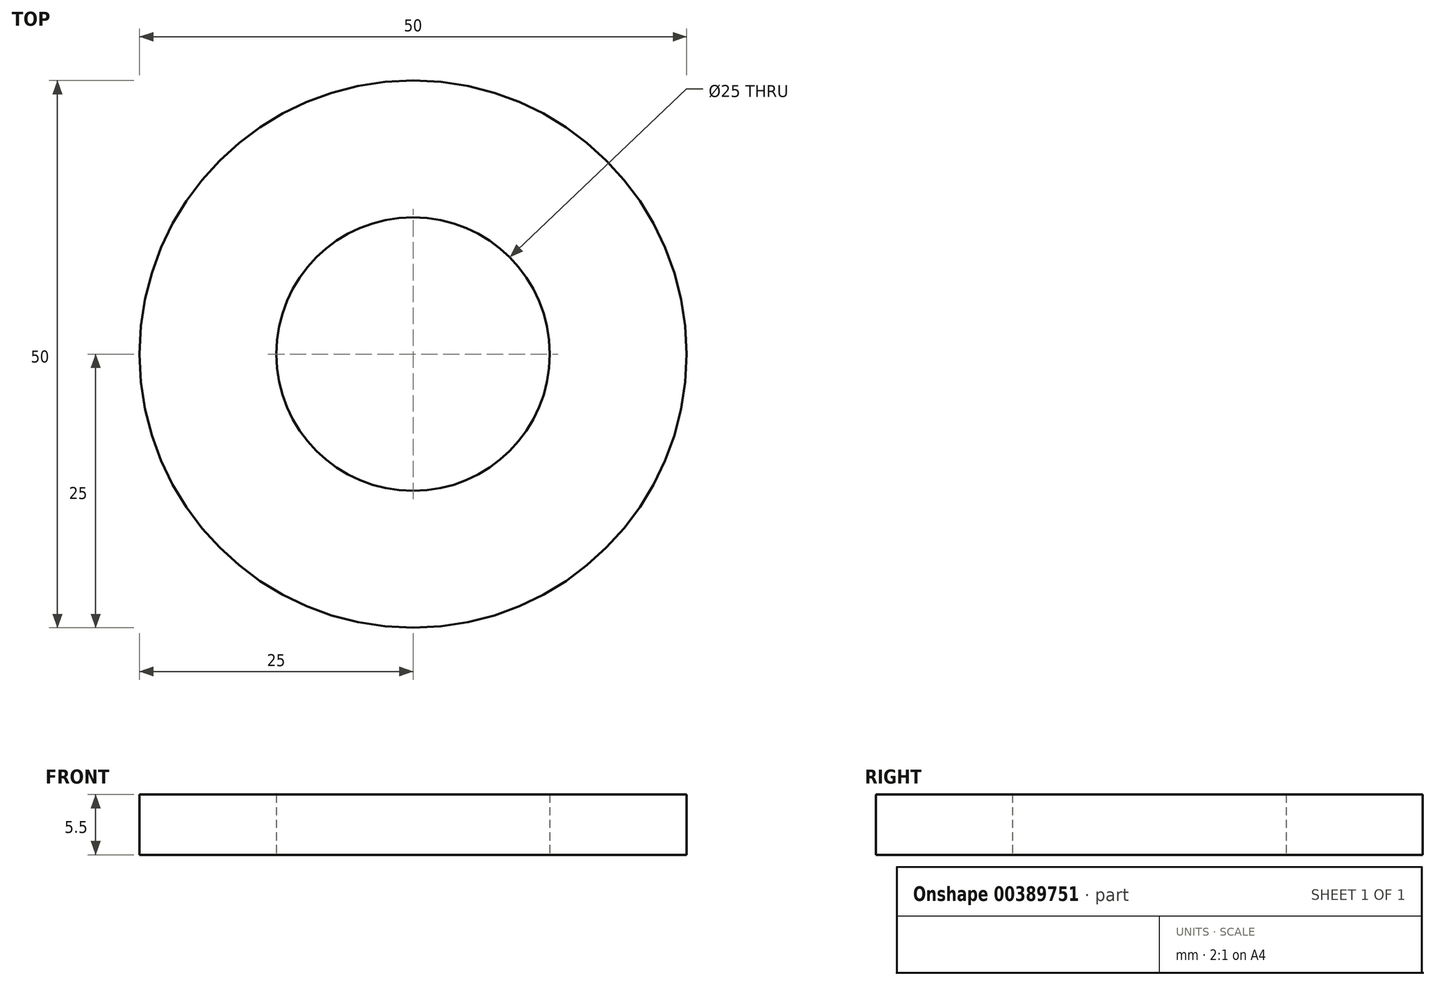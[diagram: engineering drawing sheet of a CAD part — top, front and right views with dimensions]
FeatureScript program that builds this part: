
annotation { "Feature Type Name" : "Feature", "Feature Type Description" : "" }
export const myFeature = defineFeature(function(context is Context, id is Id, definition is map)
    precondition{}
    {
        {
            var Q0;
            Q0=qCreatedBy(makeId("Top.planeOp"),FACE);
            var sketch = newSketch(context, id + "F0", { "sketchPlane" : qUnion([Q0])});
            skLineSegment(sketch, "E0.bottom", {"start": v(50, -17.5) * mm, "end": v(-50, -17.5) * mm});
            skLineSegment(sketch, "E0.top", {"start": v(50, 17.5) * mm, "end": v(-50, 17.5) * mm});
            skLineSegment(sketch, "E0.left", {"start": v(50, -17.5) * mm, "end": v(50, 17.5) * mm});
            skLineSegment(sketch, "E0.right", {"start": v(-50, -17.5) * mm, "end": v(-50, 17.5) * mm});
            skPoint(sketch, "E0.middle", {"position": v(0, 0) * mm});
            skSolve(sketch);
        }
        {
            var Q0;
            Q0=makeQuery(id+"F0.imprint","IMPRINT",FACE,{"disambiguationData":[TD([[makeQuery(id+"F0.imprint","IMPRINT",EDGE,{"derivedFrom":sQuery(id+"F0.wireOp",EDGE,"E0.bottom")}),-1.0]])]});
            extrude(context, id + "F1", {"entities" : qUnion([Q0]), "depth" : -18 * mm});
        }
        {
            var Q0;
            Q0=makeQuery(id+"F1.opExtrude","CAP_FACE",FACE,{"disambiguationData":[OSD([sQuery(id+"F0.wireOp",EDGE,"E0.bottom"),sQuery(id+"F0.wireOp",EDGE,"E0.top"),sQuery(id+"F0.wireOp",EDGE,"E0.left"),sQuery(id+"F0.wireOp",EDGE,"E0.right")])],"isStart":true});
            var sketch = newSketch(context, id + "F2", { "sketchPlane" : qUnion([Q0])});
            skCircle(sketch, "E1", {"center": v(0, 0) * mm, "radius": 12.7 * mm});
            skSolve(sketch);
        }
        {
            var Q0;
            Q0=makeQuery(id+"F2.imprint","IMPRINT",FACE,{"disambiguationData":[TD([[makeQuery(id+"F2.imprint","IMPRINT",EDGE,{"derivedFrom":sQuery(id+"F2.wireOp",EDGE,"E1")}),1.0]])]});
            extrude(context, id + "F3", {"entities" : qUnion([Q0]), "operationType" : NewBodyOperationType.ADD, "depth" : 19 * mm});
        }
        {
            var Q0;
            Q0=makeQuery(id+"F3.opExtrude","CAP_FACE",FACE,{"disambiguationData":[OSD([sQuery(id+"F2.wireOp",EDGE,"E1")])],"isStart":false});
            var sketch = newSketch(context, id + "F4", { "sketchPlane" : qUnion([Q0])});
            skCircle(sketch, "E2", {"center": v(0, 0) * mm, "radius": 25 * mm});
            skSolve(sketch);
        }
        {
            var Q0;
            Q0=makeQuery(id+"F4.imprint","IMPRINT",FACE,{"disambiguationData":[TD([[makeQuery(id+"F4.imprint","IMPRINT",EDGE,{"derivedFrom":sQuery(id+"F4.wireOp",EDGE,"E2")}),1.0]])]});
            var Q1;
            Q1=makeQuery(id+"F4.imprint","IMPRINT",FACE,{"disambiguationData":[TD([[makeQuery(id+"F4.imprint","IMPRINT",EDGE,{"derivedFrom":makeQuery(id+"F3.opExtrude","CAP_EDGE",EDGE,{"disambiguationData":[OSD([sQuery(id+"F2.wireOp",EDGE,"E1")])],"isStart":false})}),1.0]])]});
            extrude(context, id + "F5", {"entities" : qUnion([Q0, Q1]), "operationType" : NewBodyOperationType.ADD, "depth" : 5.5 * mm});
        }
        {
            var Q0;
            Q0=makeQuery(id+"F5.opExtrude","CAP_FACE",FACE,{"disambiguationData":[OSD([sQuery(id+"F4.wireOp",EDGE,"E2")])],"isStart":false});
            var sketch = newSketch(context, id + "F6", { "sketchPlane" : qUnion([Q0])});
            skCircle(sketch, "E3", {"center": v(0, 0) * mm, "radius": 2.5 * mm});
            skSolve(sketch);
        }
        {
            var Q0;
            Q0=qSketchRegion(id+"F6",true);
            extrude(context, id + "F7", {"entities" : qUnion([Q0]), "operationType" : NewBodyOperationType.ADD, "depth" : 3 * mm});
        }
        {
            var Q0;
            Q0=makeQuery(id+"F1.opExtrude","SWEPT_FACE",FACE,{"disambiguationData":[OSD([sQuery(id+"F0.wireOp",EDGE,"E0.bottom")])]});
            var sketch = newSketch(context, id + "F8", { "sketchPlane" : qUnion([Q0])});
            skLineSegment(sketch, "E4.bottom", {"start": v(-50, 0) * mm, "end": v(50, 0) * mm});
            skLineSegment(sketch, "E4.top", {"start": v(-50, -75) * mm, "end": v(50, -75) * mm});
            skLineSegment(sketch, "E4.left", {"start": v(-50, 0) * mm, "end": v(-50, -75) * mm});
            skLineSegment(sketch, "E4.right", {"start": v(50, 0) * mm, "end": v(50, -75) * mm});
            skSolve(sketch);
        }
        {
            var Q0;
            {var subQ0=sQuery(id+"F8.wireOp",EDGE,"E4.top");Q0=makeQuery(id+"F8.imprint","IMPRINT",FACE,{"disambiguationData":[TD([[makeQuery(id+"F8.imprint","IMPRINT",EDGE,{"derivedFrom":subQ0}),1.0]])]});}
            var Q1;
            {var subQ0=sQuery(id+"F8.wireOp",EDGE,"E4.bottom");Q1=makeQuery(id+"F8.imprint","IMPRINT",FACE,{"disambiguationData":[TD([[makeQuery(id+"F8.imprint","IMPRINT",EDGE,{"derivedFrom":subQ0}),1.0]])]});}
            extrude(context, id + "F9", {"entities" : qUnion([Q0, Q1]), "operationType" : NewBodyOperationType.ADD, "depth" : 12 * mm});
        }
        {
            var Q0;
            Q0=makeQuery(id+"F9.opExtrude","CAP_FACE",FACE,{"disambiguationData":[OSD([sQuery(id+"F8.wireOp",EDGE,"E4.bottom"),sQuery(id+"F8.wireOp",EDGE,"E4.top"),sQuery(id+"F8.wireOp",EDGE,"E4.left"),sQuery(id+"F8.wireOp",EDGE,"E4.right")])],"isStart":false});
            var sketch = newSketch(context, id + "F10", { "sketchPlane" : qUnion([Q0])});
            skLineSegment(sketch, "E5", {"start": v(0, 0) * mm, "end": v(-37.5, 0) * mm});
            skLineSegment(sketch, "E6", {"start": v(-37.5, 0) * mm, "end": v(-37.5, -50) * mm});
            skLineSegment(sketch, "E7", {"start": v(-37.5, -50) * mm, "end": v(37.5, -50) * mm});
            skLineSegment(sketch, "E8", {"start": v(37.5, -50) * mm, "end": v(37.5, 0) * mm});
            skLineSegment(sketch, "E9", {"start": v(37.5, 0) * mm, "end": v(0, 0) * mm});
            skLineSegment(sketch, "E10", {"start": v(50, 0) * mm, "end": v(50, -75) * mm});
            skLineSegment(sketch, "E11", {"start": v(50, -75) * mm, "end": v(-50, -75) * mm});
            skLineSegment(sketch, "E12", {"start": v(-50, -75) * mm, "end": v(-50, 0) * mm});
            skLineSegment(sketch, "E13", {"start": v(-50, 0) * mm, "end": v(50, 0) * mm});
            skSolve(sketch);
        }
        {
            var Q0;
            {var subQ2=sQuery(id+"F10.wireOp",EDGE,"E6");Q0=makeQuery(id+"F10.imprint","IMPRINT",FACE,{"disambiguationData":[TD([[makeQuery(id+"F10.imprint","IMPRINT",EDGE,{"derivedFrom":subQ2}),-1.0]])]});}
            extrude(context, id + "F11", {"entities" : qUnion([Q0]), "operationType" : NewBodyOperationType.REMOVE, "oppositeDirection" : true, "depth" : 50 * mm});
        }
        {
            var Q0;
            Q0=makeQuery(id+"F9.opExtrude","CAP_FACE",FACE,{"disambiguationData":[OSD([sQuery(id+"F8.wireOp",EDGE,"E4.bottom"),sQuery(id+"F8.wireOp",EDGE,"E4.top"),sQuery(id+"F8.wireOp",EDGE,"E4.left"),sQuery(id+"F8.wireOp",EDGE,"E4.right")])],"isStart":true});
            var sketch = newSketch(context, id + "F12", { "sketchPlane" : qUnion([Q0])});
            skLineSegment(sketch, "E14", {"start": v(37.5, -50) * mm, "end": v(37.5, -35) * mm, "construction": true});
            skLineSegment(sketch, "E15", {"start": v(37.5, -35) * mm, "end": v(22.5, -35) * mm, "construction": true});
            skLineSegment(sketch, "E16", {"start": v(22.5, -35) * mm, "end": v(-22.5, -35) * mm, "construction": true});
            skLineSegment(sketch, "E17", {"start": v(-22.5, -35) * mm, "end": v(-37.5, -35) * mm, "construction": true});
            skSolve(sketch);
        }
        {
            var Q0;
            Q0=sQuery(id+"F12.wireOp",VERTEX,"E17.start");
            var Q1;
            Q1=sQuery(id+"F12.wireOp",VERTEX,"E16.start");
            var Q2;
            Q2=makeQuery(id+"F1.opExtrude","SWEPT_BODY",BODY,{"disambiguationData":[OSD([sQuery(id+"F0.wireOp",EDGE,"E0.bottom"),sQuery(id+"F0.wireOp",EDGE,"E0.top"),sQuery(id+"F0.wireOp",EDGE,"E0.left"),sQuery(id+"F0.wireOp",EDGE,"E0.right")])]});
            hole(context, id + "F13", {"style" : HoleStyle.SIMPLE, "endStyle" : HoleEndStyle.BLIND, "holeDiameter" : 12 * mm, "holeDepth" : 12 * mm, "isTappedThrough" : true, "tappedDepth" : 12 * mm, "tapClearance" : 3, "locations" : qUnion([Q0, Q1]), "scope" : qUnion([Q2])});
        }
        {
            var Q0;
            Q0=makeQuery(id+"F1.opExtrude","SWEPT_FACE",FACE,{"disambiguationData":[OSD([sQuery(id+"F0.wireOp",EDGE,"E0.top")])]});
            var sketch = newSketch(context, id + "F14", { "sketchPlane" : qUnion([Q0])});
            skLineSegment(sketch, "E18.bottom", {"start": v(37.5, -18) * mm, "end": v(22.5, -18) * mm});
            skLineSegment(sketch, "E18.top", {"start": v(37.5, 0) * mm, "end": v(22.5, 0) * mm});
            skLineSegment(sketch, "E18.left", {"start": v(37.5, -18) * mm, "end": v(37.5, 0) * mm});
            skLineSegment(sketch, "E18.right", {"start": v(22.5, -18) * mm, "end": v(22.5, 0) * mm});
            skLineSegment(sketch, "E19.bottom", {"start": v(-37.5, 0) * mm, "end": v(-22.5, 0) * mm});
            skLineSegment(sketch, "E19.top", {"start": v(-37.5, -18) * mm, "end": v(-22.5, -18) * mm});
            skLineSegment(sketch, "E19.left", {"start": v(-37.5, 0) * mm, "end": v(-37.5, -18) * mm});
            skLineSegment(sketch, "E19.right", {"start": v(-22.5, 0) * mm, "end": v(-22.5, -18) * mm});
            skSolve(sketch);
        }
        {
            var Q0;
            Q0=makeQuery(id+"F14.imprint","IMPRINT",FACE,{"disambiguationData":[TD([[makeQuery(id+"F14.imprint","IMPRINT",EDGE,{"derivedFrom":sQuery(id+"F14.wireOp",EDGE,"E19.bottom")}),-1.0]])]});
            var Q1;
            Q1=makeQuery(id+"F14.imprint","IMPRINT",FACE,{"disambiguationData":[TD([[makeQuery(id+"F14.imprint","IMPRINT",EDGE,{"derivedFrom":sQuery(id+"F14.wireOp",EDGE,"E18.bottom")}),1.0]])]});
            extrude(context, id + "F15", {"entities" : qUnion([Q0, Q1]), "operationType" : NewBodyOperationType.REMOVE, "oppositeDirection" : true, "depth" : 35 * mm});
        }
        {
            var Q0;
            Q0=makeQuery(id+"F11.boolean.opBoolean","COPY",FACE,{"derivedFrom":makeQuery(id+"F11.opExtrude","SWEPT_FACE",FACE,{"disambiguationData":[OSD([sQuery(id+"F10.wireOp",EDGE,"E7")])]})});
            cPlane(context, id + "F16", {"entities" : qUnion([Q0]), "cplaneType" : CPlaneType.OFFSET, "offset" : 25 * mm, "width" : 150 * mm, "height" : 150 * mm});
        }
        {
            var Q0;
            Q0=qCreatedBy(id+"F16.planeOp",FACE);
            var sketch = newSketch(context, id + "F17", { "sketchPlane" : qUnion([Q0])});
            skLineSegment(sketch, "E20.bottom", {"start": v(80.64, 51.76) * mm, "end": v(-69.97, 51.76) * mm});
            skLineSegment(sketch, "E20.top", {"start": v(80.64, -50.45) * mm, "end": v(-69.97, -50.45) * mm});
            skLineSegment(sketch, "E20.left", {"start": v(80.64, 51.76) * mm, "end": v(80.64, -50.45) * mm});
            skLineSegment(sketch, "E20.right", {"start": v(-69.97, 51.76) * mm, "end": v(-69.97, -50.45) * mm});
            skSolve(sketch);
        }
        {
            var Q0;
            Q0=makeQuery(id+"F17.imprint","IMPRINT",FACE,{"disambiguationData":[TD([[makeQuery(id+"F17.imprint","IMPRINT",EDGE,{"derivedFrom":sQuery(id+"F17.wireOp",EDGE,"E20.bottom")}),1.0]])]});
            extrude(context, id + "F18", {"entities" : qUnion([Q0]), "operationType" : NewBodyOperationType.REMOVE, "oppositeDirection" : true, "depth" : 94 * mm});
        }
        {
            var Q0;
            Q0=makeQuery(id+"F18.boolean.opBoolean","MERGE",FACE,{"derivedFrom":[makeQuery(id+"F5.opExtrude","CAP_FACE",FACE,{"disambiguationData":[OSD([sQuery(id+"F4.wireOp",EDGE,"E2")])],"isStart":true}),makeQuery(id+"F18.opExtrude","CAP_FACE",FACE,{"disambiguationData":[OSD([sQuery(id+"F17.wireOp",EDGE,"E20.bottom"),sQuery(id+"F17.wireOp",EDGE,"E20.top"),sQuery(id+"F17.wireOp",EDGE,"E20.left"),sQuery(id+"F17.wireOp",EDGE,"E20.right")])],"isStart":false})]});
            var sketch = newSketch(context, id + "F19", { "sketchPlane" : qUnion([Q0])});
            skCircle(sketch, "E21", {"center": v(0, 0) * mm, "radius": 12.5 * mm});
            skSolve(sketch);
        }
        {
            var Q0;
            Q0=makeQuery(id+"F19.imprint","IMPRINT",FACE,{"disambiguationData":[TD([[makeQuery(id+"F19.imprint","IMPRINT",EDGE,{"derivedFrom":sQuery(id+"F19.wireOp",EDGE,"E21")}),1.0]])]});
            extrude(context, id + "F20", {"entities" : qUnion([Q0]), "operationType" : NewBodyOperationType.REMOVE, "oppositeDirection" : true, "depth" : 25 * mm});
        }
    });
